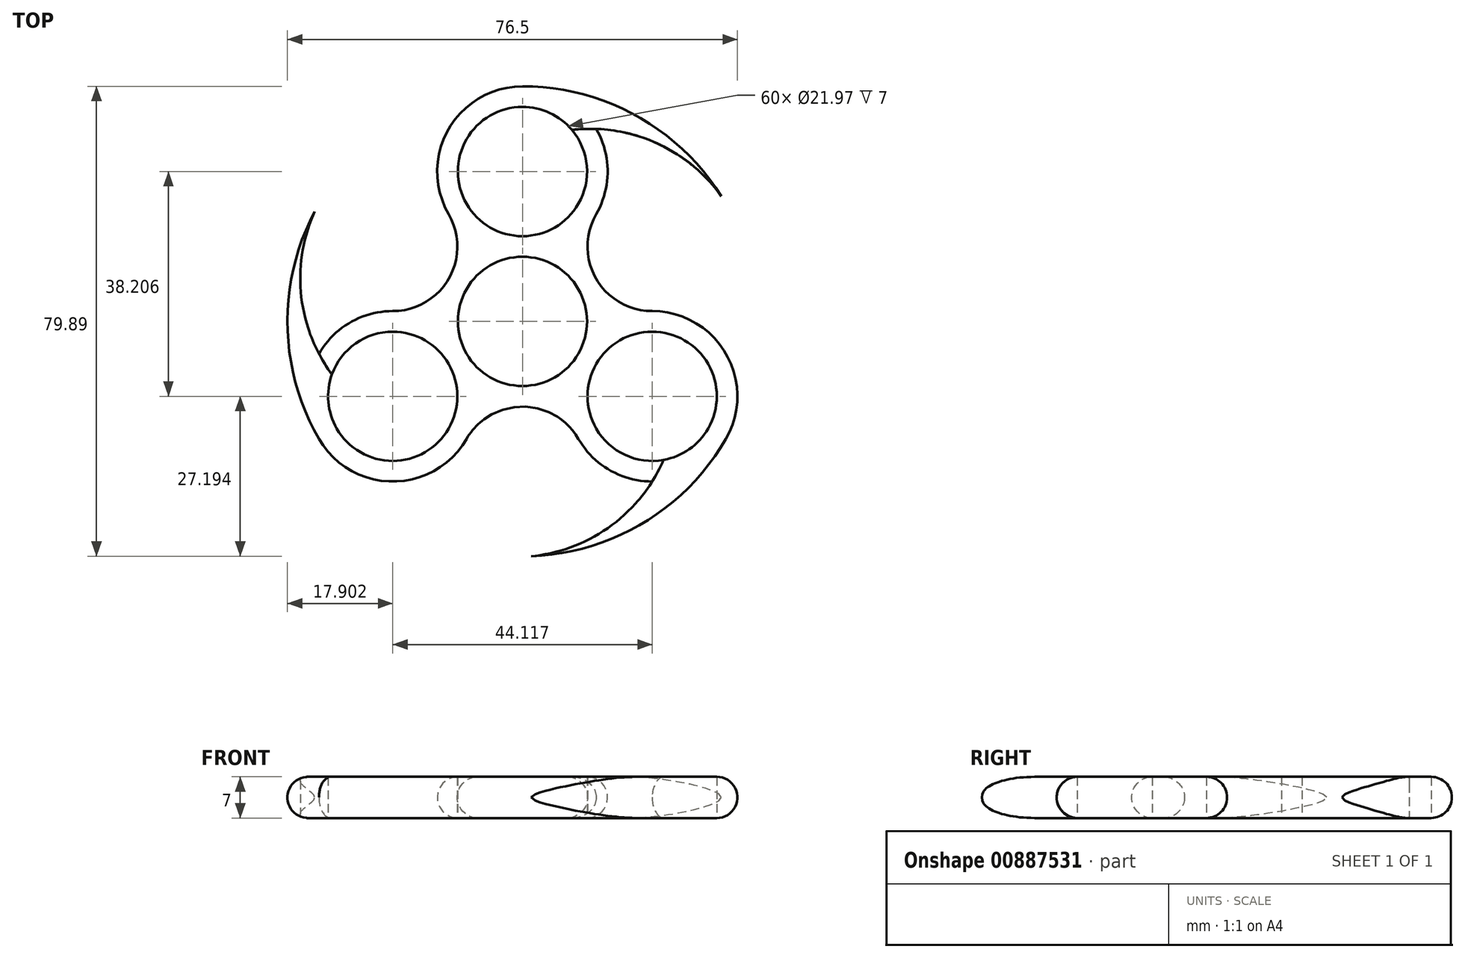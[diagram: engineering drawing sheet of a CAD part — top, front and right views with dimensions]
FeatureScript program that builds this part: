
annotation { "Feature Type Name" : "Feature", "Feature Type Description" : "" }
export const myFeature = defineFeature(function(context is Context, id is Id, definition is map)
    precondition{}
    {
        {
            var Q0;
            Q0=qCreatedBy(makeId("Top.planeOp"),FACE);
            var sketch = newSketch(context, id + "F0", { "sketchPlane" : qUnion([Q0])});
            skCircle(sketch, "E0", {"center": v(0, 0) * mm, "radius": 10.99 * mm});
            skCircle(sketch, "E1", {"center": v(0, 0) * mm, "radius": 25.47 * mm, "construction": true});
            skCircle(sketch, "E2", {"center": v(0, 25.47) * mm, "radius": 10.99 * mm});
            skCircle(sketch, "E3", {"center": v(-22.06, -12.74) * mm, "radius": 10.99 * mm});
            skCircle(sketch, "E4", {"center": v(22.06, -12.74) * mm, "radius": 10.99 * mm});
            skLineSegment(sketch, "E5", {"start": v(-22.06, -12.74) * mm, "end": v(22.06, -12.74) * mm, "construction": true});
            skLineSegment(sketch, "E6", {"start": v(0, 25.47) * mm, "end": v(-22.06, -12.74) * mm, "construction": true});
            skLineSegment(sketch, "E7", {"start": v(22.06, -12.74) * mm, "end": v(0, 25.47) * mm, "construction": true});
            skLineSegment(sketch, "E8.bottom", {"start": v(-57.15, 57.15) * mm, "end": v(57.15, 57.15) * mm, "construction": true});
            skLineSegment(sketch, "E8.top", {"start": v(-57.15, -57.15) * mm, "end": v(57.15, -57.15) * mm, "construction": true});
            skLineSegment(sketch, "E8.left", {"start": v(-57.15, 57.15) * mm, "end": v(-57.15, -57.15) * mm, "construction": true});
            skLineSegment(sketch, "E8.right", {"start": v(57.15, 57.15) * mm, "end": v(57.15, -57.15) * mm, "construction": true});
            skPoint(sketch, "E9", {"position": v(-57.15, 0) * mm});
            skPoint(sketch, "E10", {"position": v(0, 57.15) * mm});
            skSolve(sketch);
        }
        {
            var Q0;
            Q0=qCreatedBy(makeId("Top.planeOp"),FACE);
            var sketch = newSketch(context, id + "F1", { "sketchPlane" : qUnion([Q0])});
            skCircle(sketch, "E11", {"center": v(0, 0) * mm, "radius": 10.99 * mm});
            skCircle(sketch, "E12", {"center": v(-22.06, -12.74) * mm, "radius": 10.99 * mm});
            skCircle(sketch, "E13", {"center": v(0, 25.47) * mm, "radius": 10.99 * mm});
            skCircle(sketch, "E14", {"center": v(22.06, -12.74) * mm, "radius": 10.99 * mm});
            skLineSegment(sketch, "E15.bottom", {"start": v(-57.15, 57.15) * mm, "end": v(57.15, 57.15) * mm, "construction": true});
            skLineSegment(sketch, "E15.top", {"start": v(-57.15, -57.15) * mm, "end": v(57.15, -57.15) * mm, "construction": true});
            skLineSegment(sketch, "E15.left", {"start": v(-57.15, 57.15) * mm, "end": v(-57.15, -57.15) * mm, "construction": true});
            skLineSegment(sketch, "E15.right", {"start": v(57.15, 57.15) * mm, "end": v(57.15, -57.15) * mm, "construction": true});
            skPoint(sketch, "E16", {"position": v(-57.15, 0) * mm});
            skPoint(sketch, "E17", {"position": v(0, 57.15) * mm});
            skArc(sketch, "E18", {"start": v(-22.06, 1.75) * mm, "mid": v(-29.3, -0.2) * mm, "end": v(-34.6, -5.5) * mm});
            skArc(sketch, "E19", {"start": v(12.54, 18.23) * mm, "mid": v(14.49, 25.47) * mm, "end": v(12.54, 32.71) * mm});
            skArc(sketch, "E20", {"start": v(9.51, -19.98) * mm, "mid": v(14.82, -25.28) * mm, "end": v(22.06, -27.22) * mm});
            skArc(sketch, "E21", {"start": v(-22.06, 1.75) * mm, "mid": v(-12.54, 7.24) * mm, "end": v(-12.54, 18.23) * mm});
            skArc(sketch, "E22", {"start": v(12.54, 18.23) * mm, "mid": v(12.54, 7.24) * mm, "end": v(22.06, 1.75) * mm});
            skArc(sketch, "E23", {"start": v(9.51, -19.98) * mm, "mid": v(0, -14.49) * mm, "end": v(-9.51, -19.98) * mm});
            skCircle(sketch, "E24", {"center": v(0, 0) * mm, "radius": 14.49 * mm, "construction": true});
            skArc(sketch, "E25", {"start": v(33.84, 21.25) * mm, "mid": v(19.33, 34.97) * mm, "end": v(0, 39.96) * mm});
            skCircle(sketch, "E26", {"center": v(0, 0) * mm, "radius": 39.96 * mm, "construction": true});
            skArc(sketch, "E27", {"start": v(33.84, 21.25) * mm, "mid": v(24.52, 29.46) * mm, "end": v(12.54, 32.71) * mm});
            skArc(sketch, "E28.1.0", {"start": v(-35.32, 18.68) * mm, "mid": v(-39.95, -0.74) * mm, "end": v(-34.6, -19.98) * mm});
            skArc(sketch, "E28.1.1", {"start": v(-35.32, 18.68) * mm, "mid": v(-37.77, 6.5) * mm, "end": v(-34.6, -5.5) * mm});
            skArc(sketch, "E28.2.0", {"start": v(1.49, -39.93) * mm, "mid": v(20.62, -34.23) * mm, "end": v(34.6, -19.98) * mm});
            skArc(sketch, "E28.2.1", {"start": v(1.49, -39.93) * mm, "mid": v(13.25, -35.97) * mm, "end": v(22.06, -27.22) * mm});
            skArc(sketch, "E29.trimOffspring", {"start": v(0, 39.96) * mm, "mid": v(-12.54, 32.71) * mm, "end": v(-12.54, 18.23) * mm});
            skArc(sketch, "E30.trimOffspring", {"start": v(-34.6, -19.98) * mm, "mid": v(-22.06, -27.22) * mm, "end": v(-9.51, -19.98) * mm});
            skArc(sketch, "E31.trimOffspring", {"start": v(34.6, -19.98) * mm, "mid": v(34.6, -5.5) * mm, "end": v(22.06, 1.75) * mm});
            skSolve(sketch);
        }
        {
            var Q0;
            Q0 = qSketchRegion(id + "F1", true);
            extrude(context, id + "F2", {"entities" : qUnion([Q0]), "depth" : 7 * mm, "offsetDistance" : 25.4 * mm});
        }
        {
            var Q0;
            Q0=makeQuery(id+"F2.opExtrude","CAP_EDGE",EDGE,{"disambiguationData":[OSD([sQuery(id+"F1.wireOp",EDGE,"E23")])],"isStart":false});
            var Q1;
            Q1=makeQuery(id+"F2.opExtrude","CAP_EDGE",EDGE,{"disambiguationData":[OSD([sQuery(id+"F1.wireOp",EDGE,"E31.trimOffspring")])],"isStart":false});
            var Q2;
            Q2=makeQuery(id+"F2.opExtrude","CAP_EDGE",EDGE,{"disambiguationData":[OSD([sQuery(id+"F1.wireOp",EDGE,"E21")])],"isStart":false});
            var Q3;
            Q3=makeQuery(id+"F2.opExtrude","CAP_EDGE",EDGE,{"disambiguationData":[OSD([sQuery(id+"F1.wireOp",EDGE,"E22")])],"isStart":true});
            var Q4;
            Q4=makeQuery(id+"F2.opExtrude","CAP_EDGE",EDGE,{"disambiguationData":[OSD([sQuery(id+"F1.wireOp",EDGE,"E21")])],"isStart":true});
            var Q5;
            Q5=makeQuery(id+"F2.opExtrude","CAP_EDGE",EDGE,{"disambiguationData":[OSD([sQuery(id+"F1.wireOp",EDGE,"E23")])],"isStart":true});
            fillet(context, id + "F3", {"entities" : qUnion([Q0, Q1, Q2, Q3, Q4, Q5]), "radius" : 3.5 * mm, "tangentPropagation" : true, "allowEdgeOverflow" : false});
        }
    });
